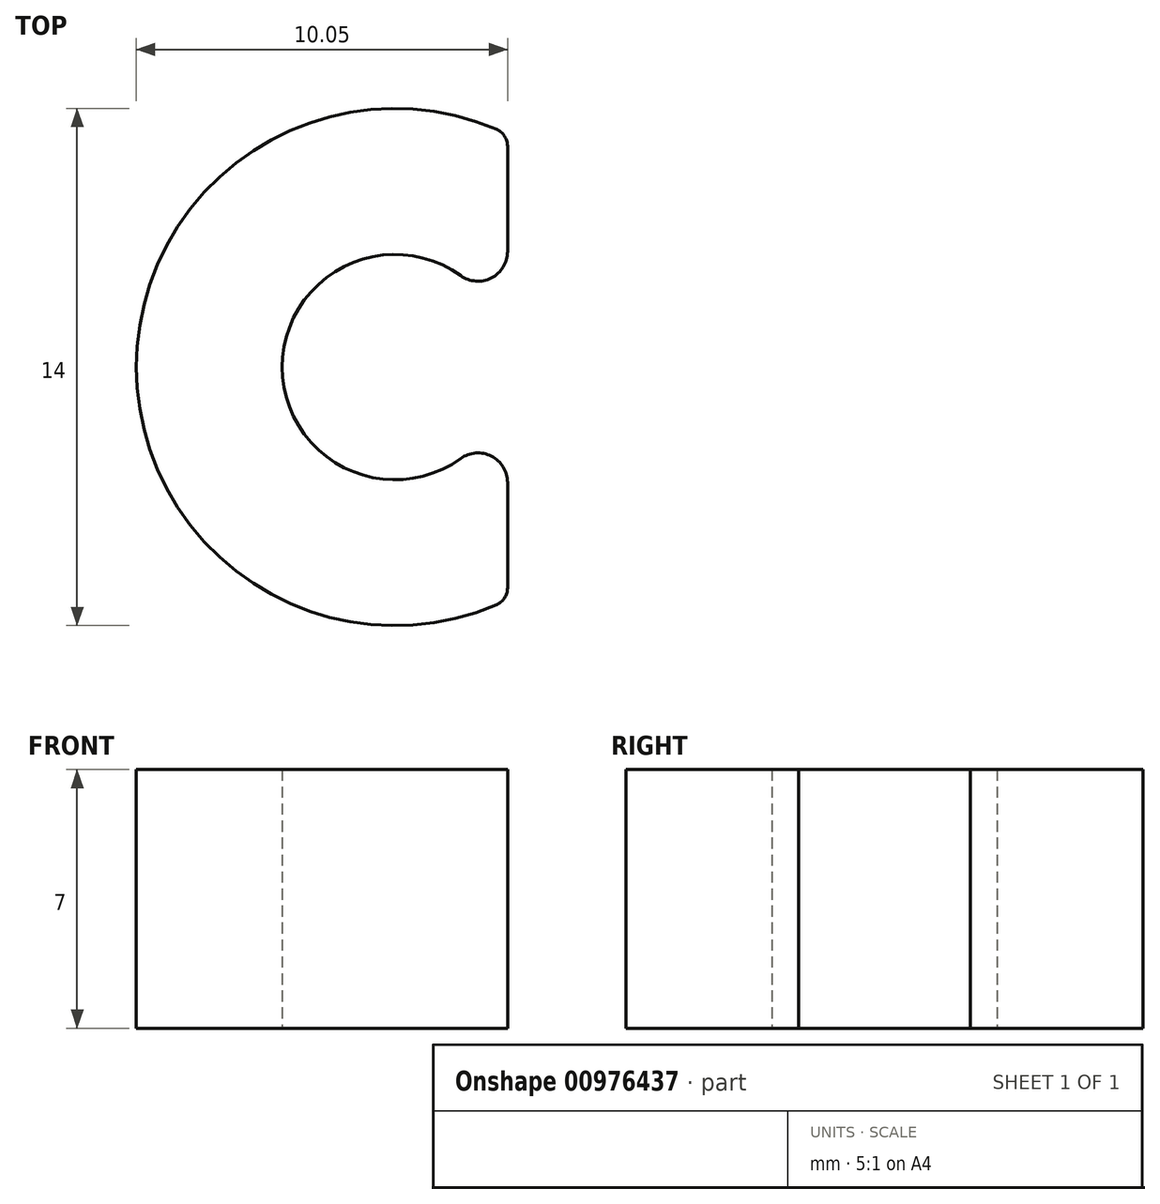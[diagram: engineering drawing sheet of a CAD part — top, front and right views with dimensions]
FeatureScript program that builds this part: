
annotation { "Feature Type Name" : "Feature", "Feature Type Description" : "" }
export const myFeature = defineFeature(function(context is Context, id is Id, definition is map)
    precondition{}
    {
        {
            var Q0;
            Q0=qCreatedBy(makeId("Top.planeOp"),FACE);
            var sketch = newSketch(context, id + "F0", { "sketchPlane" : qUnion([Q0])});
            skArc(sketch, "E0", {"start": v(1.78, 2.48) * mm, "mid": v(-3.05, 0) * mm, "end": v(1.78, -2.48) * mm});
            skArc(sketch, "E1", {"start": v(2.74, 6.44) * mm, "mid": v(-7, 0) * mm, "end": v(2.74, -6.44) * mm});
            skLineSegment(sketch, "E2", {"start": v(3.05, 5.98) * mm, "end": v(3.05, 3.13) * mm});
            skLineSegment(sketch, "E3.trimOffspring", {"start": v(3.05, -3.13) * mm, "end": v(3.05, -5.98) * mm});
            skPoint(sketch, "E4.visualSharp", {"position": v(3.05, 6.3) * mm});
            skArc(sketch, "E4.filletArc", {"start": v(3.05, 5.98) * mm, "mid": v(2.97, 6.26) * mm, "end": v(2.74, 6.44) * mm});
            skPoint(sketch, "E5.visualSharp", {"position": v(3.05, 0.1) * mm});
            skArc(sketch, "E5.filletArc", {"start": v(1.78, 2.48) * mm, "mid": v(2.61, 2.41) * mm, "end": v(3.05, 3.13) * mm});
            skArc(sketch, "E6.filletArc", {"start": v(3.05, -3.13) * mm, "mid": v(2.61, -2.41) * mm, "end": v(1.78, -2.48) * mm});
            skPoint(sketch, "E7.visualSharp", {"position": v(3.05, -6.3) * mm});
            skArc(sketch, "E7.filletArc", {"start": v(2.74, -6.44) * mm, "mid": v(2.97, -6.26) * mm, "end": v(3.05, -5.98) * mm});
            skLineSegment(sketch, "E8", {"start": v(2.55, 5.98) * mm, "end": v(2.25, -3.13) * mm, "construction": true});
            skSolve(sketch);
        }
        {
            var Q0;
            Q0 = qSketchRegion(id + "F0", true);
            extrude(context, id + "F1", {"entities" : qUnion([Q0]), "depth" : 7 * mm, "offsetDistance" : 25 * mm});
        }
    });
